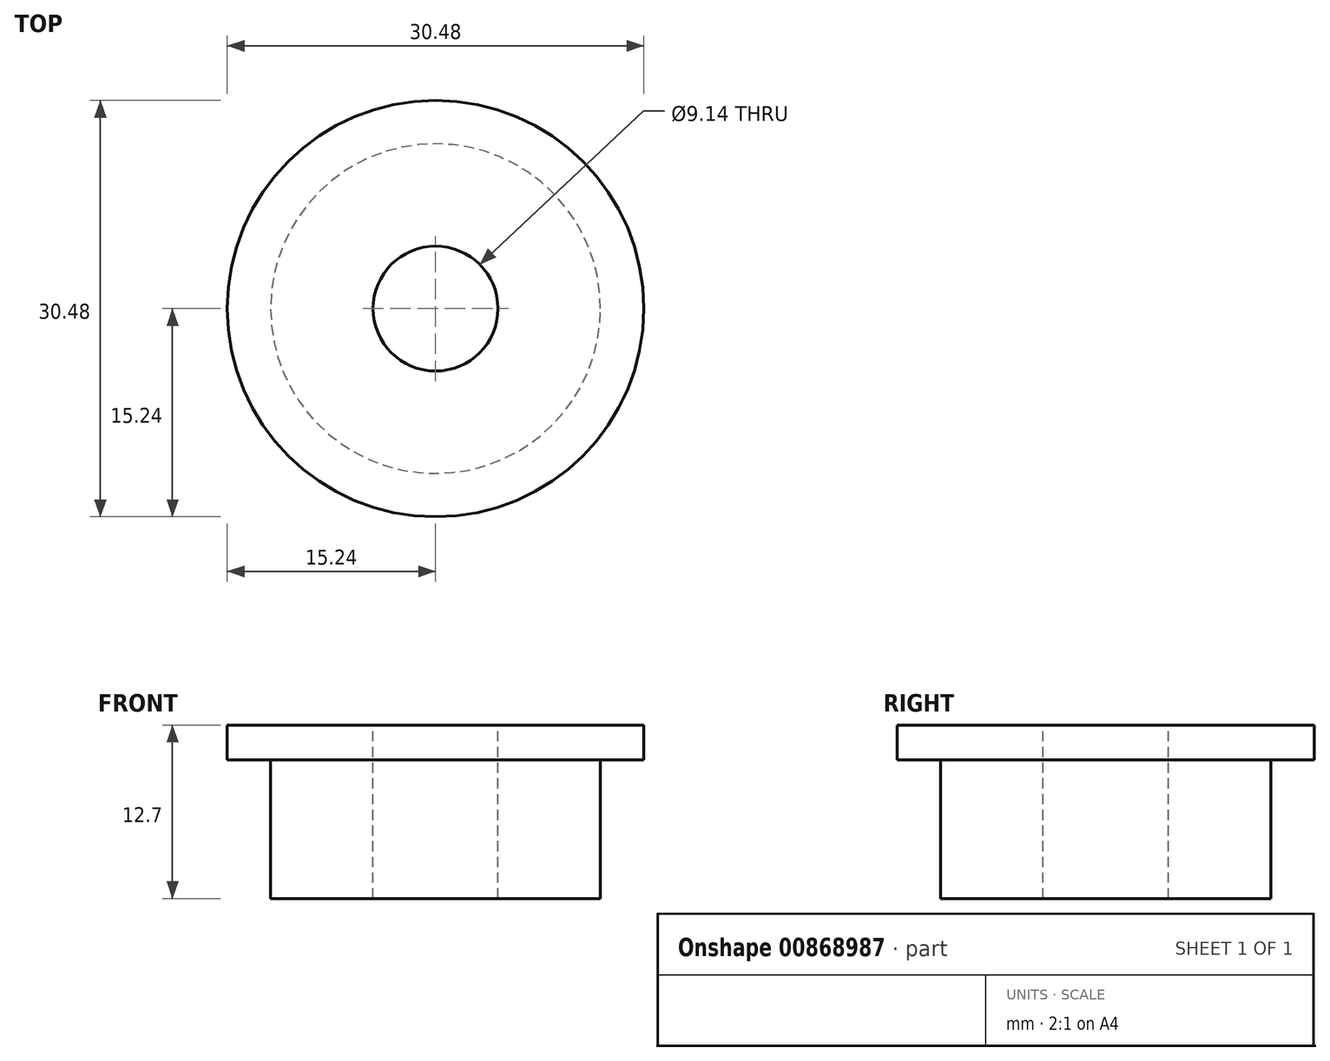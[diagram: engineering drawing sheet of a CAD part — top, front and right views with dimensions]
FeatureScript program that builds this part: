
annotation { "Feature Type Name" : "Feature", "Feature Type Description" : "" }
export const myFeature = defineFeature(function(context is Context, id is Id, definition is map)
    precondition{}
    {
        {
            var Q0;
            Q0=qCreatedBy(makeId("Top.planeOp"),FACE);
            var sketch = newSketch(context, id + "F0", { "sketchPlane" : qUnion([Q0])});
            skCircle(sketch, "E0", {"center": v(0, 0) * mm, "radius": 12.07 * mm});
            skSolve(sketch);
        }
        {
            var Q0;
            Q0=qSketchRegion(id+"F0",true);
            extrude(context, id + "F1", {"entities" : qUnion([Q0]), "depth" : 10.16 * mm, "offsetDistance" : 25.4 * mm});
        }
        {
            var Q0;
            Q0=makeQuery(id+"F1.opExtrude","CAP_FACE",FACE,{"disambiguationData":[OSD([sQuery(id+"F0.wireOp",EDGE,"E0")])],"isStart":false});
            var sketch = newSketch(context, id + "F2", { "sketchPlane" : qUnion([Q0])});
            skCircle(sketch, "E1", {"center": v(0, 0) * mm, "radius": 15.24 * mm});
            skSolve(sketch);
        }
        {
            var Q0;
            Q0=qSketchRegion(id+"F2",true);
            extrude(context, id + "F3", {"entities" : qUnion([Q0]), "operationType" : NewBodyOperationType.ADD, "depth" : 2.54 * mm, "offsetDistance" : 25.4 * mm});
        }
        {
            var Q0;
            Q0=makeQuery(id+"F3.opExtrude","CAP_FACE",FACE,{"disambiguationData":[OSD([sQuery(id+"F2.wireOp",EDGE,"E1")])],"isStart":false});
            var sketch = newSketch(context, id + "F4", { "sketchPlane" : qUnion([Q0])});
            skCircle(sketch, "E2", {"center": v(0, 0) * mm, "radius": 4.57 * mm});
            skSolve(sketch);
        }
        {
            var Q0;
            Q0=qSketchRegion(id+"F4",true);
            extrude(context, id + "F5", {"entities" : qUnion([Q0]), "operationType" : NewBodyOperationType.REMOVE, "oppositeDirection" : true, "depth" : 25.4 * mm, "offsetDistance" : 25.4 * mm});
        }
    });
